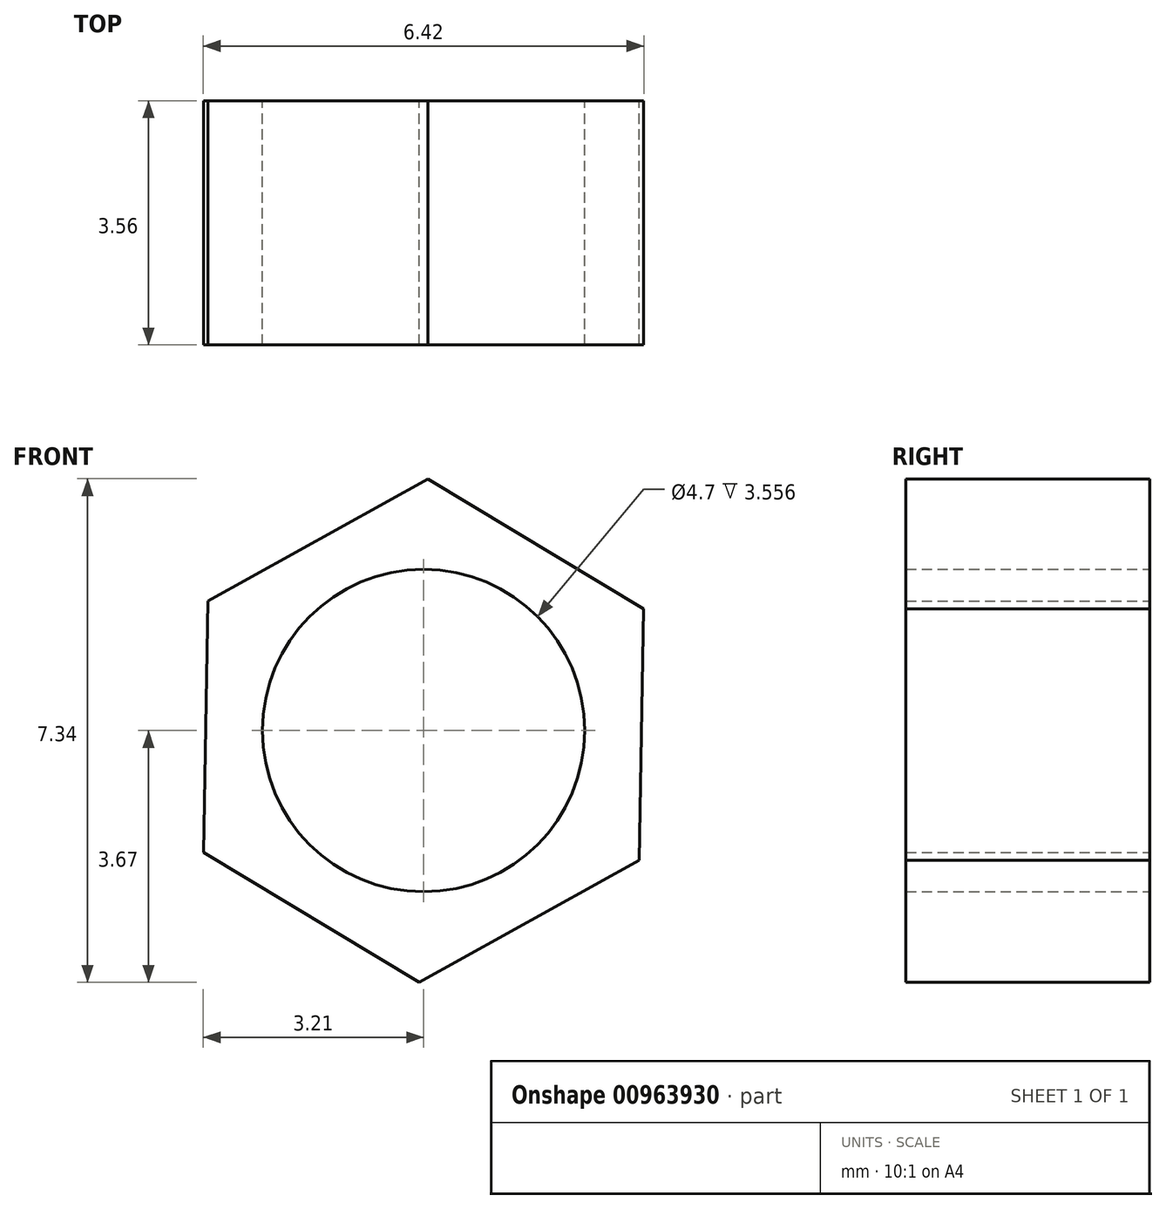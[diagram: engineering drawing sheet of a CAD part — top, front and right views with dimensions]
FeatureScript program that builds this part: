
annotation { "Feature Type Name" : "Feature", "Feature Type Description" : "" }
export const myFeature = defineFeature(function(context is Context, id is Id, definition is map)
    precondition{}
    {
        {
            var Q0;
            Q0=qCreatedBy(makeId("Front.planeOp"),FACE);
            var sketch = newSketch(context, id + "F0", { "sketchPlane" : qUnion([Q0])});
            skCircle(sketch, "E0.cCircle", {"center": v(0, 0) * mm, "radius": 3.18 * mm, "construction": true});
            skLineSegment(sketch, "E0.0", {"start": v(0.07, 3.67) * mm, "end": v(3.2, 1.78) * mm});
            skLineSegment(sketch, "E0.1", {"start": v(3.2, 1.78) * mm, "end": v(3.14, -1.9) * mm});
            skLineSegment(sketch, "E0.2", {"start": v(3.14, -1.9) * mm, "end": v(-0.07, -3.67) * mm});
            skLineSegment(sketch, "E0.3", {"start": v(-0.07, -3.67) * mm, "end": v(-3.2, -1.78) * mm});
            skLineSegment(sketch, "E0.4", {"start": v(-3.2, -1.78) * mm, "end": v(-3.14, 1.9) * mm});
            skLineSegment(sketch, "E0.5", {"start": v(-3.14, 1.9) * mm, "end": v(0.07, 3.67) * mm});
            skPoint(sketch, "E0.0.midPoint", {"position": v(1.64, 2.72) * mm});
            skCircle(sketch, "E1", {"center": v(0, 0) * mm, "radius": 2.35 * mm});
            skSolve(sketch);
        }
        {
            var Q0;
            Q0=makeQuery(id+"F0.imprint","IMPRINT",FACE,{"disambiguationData":[TD([[makeQuery(id+"F0.imprint","IMPRINT",EDGE,{"derivedFrom":sQuery(id+"F0.wireOp",EDGE,"E0.0")}),-1.0]])]});
            extrude(context, id + "F1", {"entities" : qUnion([Q0]), "depth" : 3.56 * mm, "offsetDistance" : 25.4 * mm});
        }
    });
